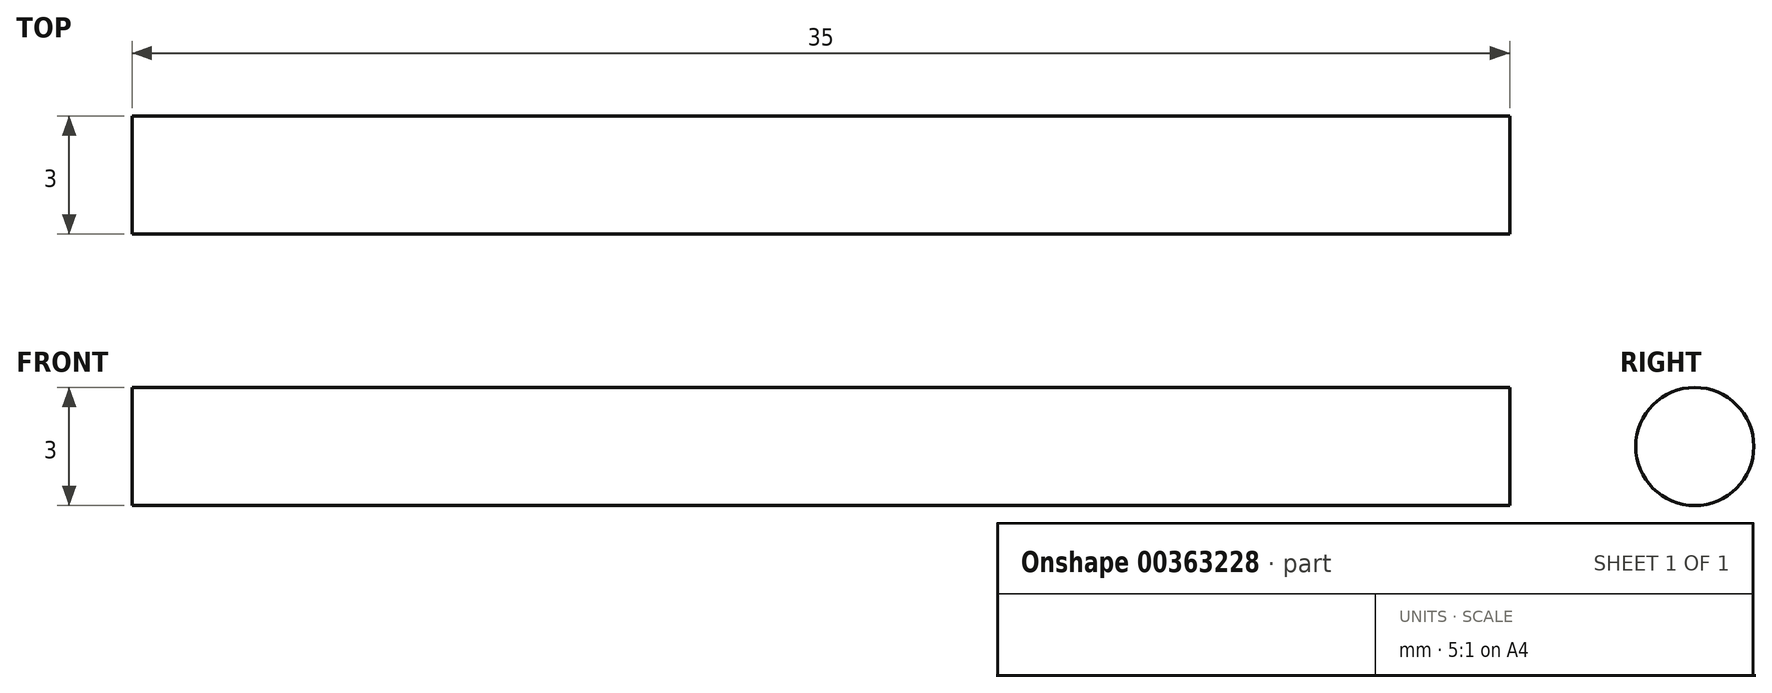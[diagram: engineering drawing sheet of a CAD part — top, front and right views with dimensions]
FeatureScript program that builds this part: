
annotation { "Feature Type Name" : "Feature", "Feature Type Description" : "" }
export const myFeature = defineFeature(function(context is Context, id is Id, definition is map)
    precondition{}
    {
        {
            var Q0;
            Q0=qCreatedBy(makeId("Right.planeOp"),FACE);
            var sketch = newSketch(context, id + "F0", { "sketchPlane" : qUnion([Q0])});
            skCircle(sketch, "E0", {"center": v(0, 0) * mm, "radius": 1.5 * mm});
            skSolve(sketch);
        }
        {
            var Q0;
            Q0 = qSketchRegion(id + "F0", true);
            extrude(context, id + "F1", {"entities" : qUnion([Q0]), "endBound" : BoundingType.SYMMETRIC, "depth" : 35 * mm});
        }
    });
